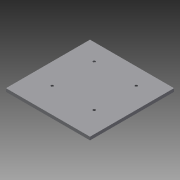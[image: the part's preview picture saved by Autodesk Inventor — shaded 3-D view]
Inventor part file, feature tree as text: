
AUTODESK INVENTOR PART (.ipt)
format: ipt  version: 2013 (Build 170138000, 138)  size: 84,992 bytes
history: native  units: in
note: dims shown in document units (in); Inventor stores cm internally (conversion verified against a paired STEP export)
features: extrude x1, hole x1, sketch x1
ambient origin geometry x8: Origin, YZ Plane, XZ Plane, XY Plane, X Axis, Y Axis, Z Axis, Center Point
bodies: Solid1 (feature_tree)
feature tree (3):
  extrude  "Extrusion1"  Depth=5.0in
  hole  "Hole1"  [1 undecoded]
  sketch  "Sketch2"  dims[d0=5.0in d1=5.0in d2=0.1875in d3=0.0in d4=2.5in d6=1.25in d8=1.25in d9=2.5in d10=1.0in d11=0.145in d12=0.75in d13=0.375in d14=0.25in d15=0.5635in d16=1.0in d17=0.8108in]
note: 1 required parameter value undecoded (feature->parameter linkage not recoverable at this tier; creation-order binding heuristic only, values carry confidence <= 0.55)
